# Revit family: xUrinal-Wall_Hung-American Standard-Pintbrook-6002.001
name_source: partatom
category: Plumbing Fixtures
revit_build: Autodesk Revit 2014 (Build: 20130308_1515(x64)
units: mm (PartAtom-declared; Revit-internal decimal feet)

## types (1)
- 6002.001
    ADA Compliant = Yes
    Assembly Code = D2010210
    CW Connection = Yes
    CWFU = 5
    Cold Water Connection Diameter = 3/4"
    Cold Water Connection Height = 11 1/2"
    Cold Water Connection Width = 4 3/4"
    Default Elevation = 17"
    Description = American Standard Pintbrook Urinal
    Flush Rate = 0.125 gpf/0.50 gpf (0.47 Lpf/1.9 Lpf)
    HW Connection = No
    HWFU = 0
    Height = 22 5/8"
    High Efficiency = Yes
    Installation Type = Wall Hung
    Length = 14 7/16"
    Manufacturer = American Standard
    Material = Vitreous China-American Standard-001-White
    Model = 6002.001
    Price = Prices may vary. Please consult Manufacturer Representative for most up-to-date price list.
    Product Page URL = http://www.americanstandard-us.com
    Spud Location = Top Spud
    Type Comments = Recommended working pressure between 20 psi at valve when flushing and 80 psi static.
    URL = http://www.americanstandard-us.com
    Vent Connection = No
    WFU = 5
    Warranty Information = 1 Year Limited Warranty
    Waste Connection = Yes
    Waste Connection Diameter = 2"
    Waste Connection Height = 5 1/2"
    Width = 14 5/16"

## geometry (parser evidence)
native form markers: Sweep x1
no freeform markers — native parametric forms only
